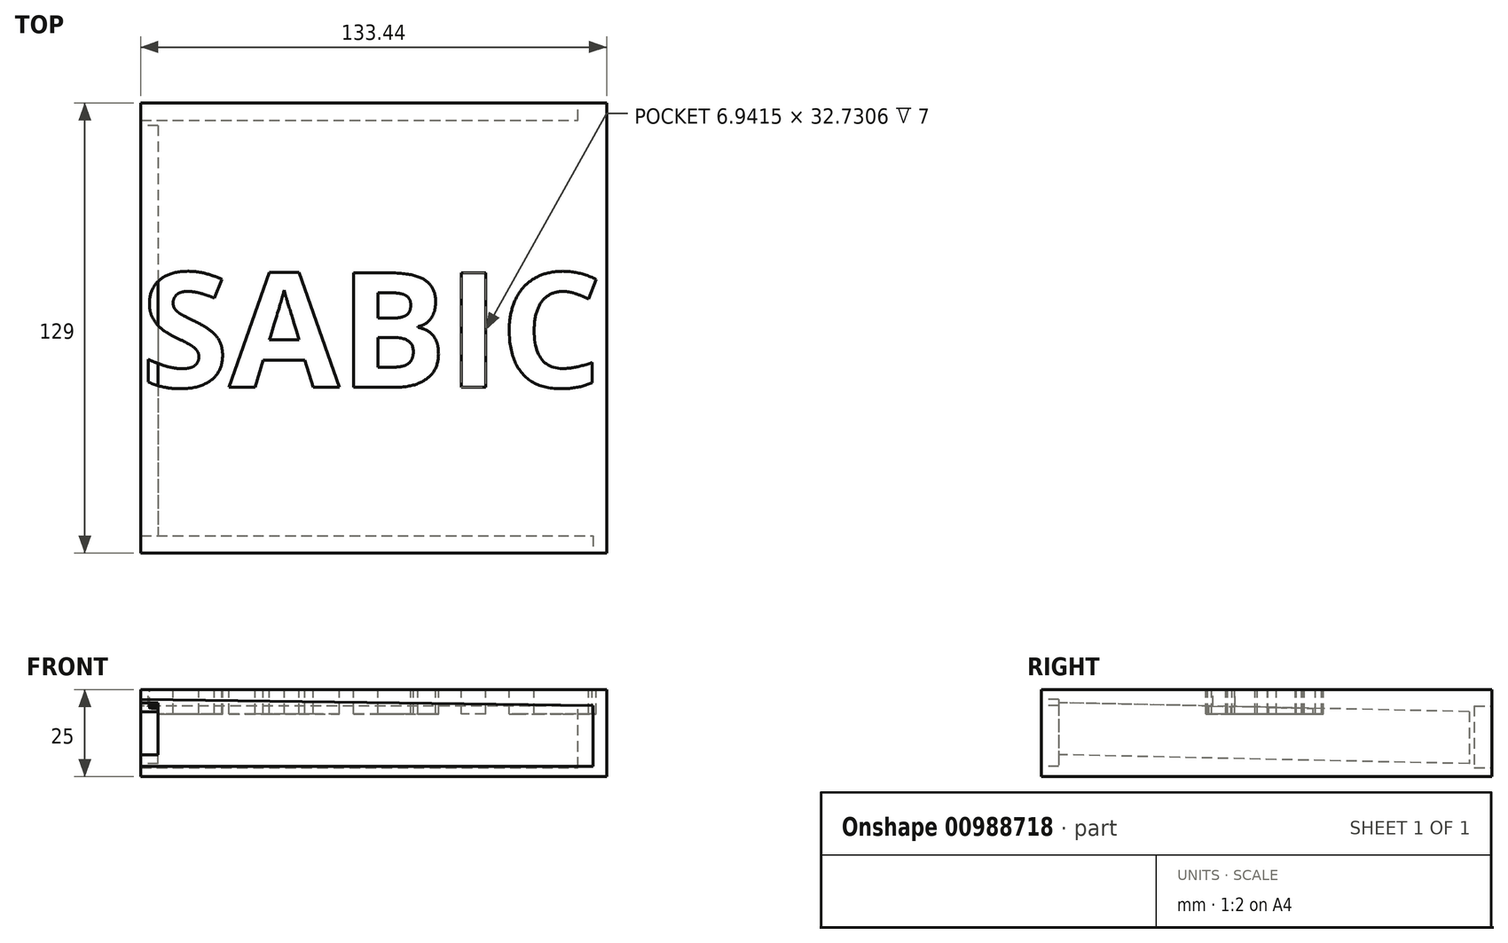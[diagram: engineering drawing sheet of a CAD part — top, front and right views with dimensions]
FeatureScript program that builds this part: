
annotation { "Feature Type Name" : "Feature", "Feature Type Description" : "" }
export const myFeature = defineFeature(function(context is Context, id is Id, definition is map)
    precondition{}
    {
        {
            var Q0;
            Q0=qCreatedBy(makeId("Top.planeOp"),FACE);
            var sketch = newSketch(context, id + "F0", { "sketchPlane" : qUnion([Q0])});
            skLineSegment(sketch, "E0.bottom", {"start": v(63.41, 63.62) * mm, "end": v(-70.03, 63.62) * mm});
            skLineSegment(sketch, "E0.top", {"start": v(63.41, -65.38) * mm, "end": v(-70.03, -65.38) * mm});
            skLineSegment(sketch, "E0.left", {"start": v(63.41, 63.62) * mm, "end": v(63.41, -65.38) * mm});
            skLineSegment(sketch, "E0.right", {"start": v(-70.03, 63.62) * mm, "end": v(-70.03, -65.38) * mm});
            skLineSegment(sketch, "E1", {"start": v(0, 63.62) * mm, "end": v(0, -65.38) * mm});
            skSolve(sketch);
        }
        {
            var Q0;
            Q0 = qSketchRegion(id + "F0", true);
            extrude(context, id + "F1", {"entities" : qUnion([Q0]), "depth" : 25 * mm, "offsetDistance" : 25 * mm});
        }
        {
            var Q0;
            Q0=makeQuery(id+"F1.opExtrude","CAP_FACE",FACE,{"disambiguationData":[OSD([sQuery(id+"F0.wireOp",EDGE,"E0.bottom"),sQuery(id+"F0.wireOp",EDGE,"E0.top"),sQuery(id+"F0.wireOp",EDGE,"E0.left"),sQuery(id+"F0.wireOp",EDGE,"E0.right")])],"isStart":false});
            var sketch = newSketch(context, id + "F2", { "sketchPlane" : qUnion([Q0])});
            skText(sketch, "E2", { "text": "SABIC", "fontName": "OpenSans-Bold.ttf"});
            const initialGuessF2  = {"E2": [-0.07003, -0.01781, 1, 0, 0.03301]};
            skSetInitialGuess(sketch, initialGuessF2);
            skSolve(sketch);
        }
        {
            var Q0;
            Q0 = qSketchRegion(id + "F2", true);
            extrude(context, id + "F3", {"entities" : qUnion([Q0]), "operationType" : NewBodyOperationType.REMOVE, "oppositeDirection" : true, "depth" : 7 * mm, "offsetDistance" : 25 * mm});
        }
        {
            var Q0;
            Q0=makeQuery(id+"F1.opExtrude","SWEPT_FACE",FACE,{"disambiguationData":[OSD([sQuery(id+"F0.wireOp",EDGE,"E0.right")])]});
            var sketch = newSketch(context, id + "F4", { "sketchPlane" : qUnion([Q0])});
            skSolve(sketch);
        }
        {
            var Q0;
            Q0=makeQuery(id+"F1.opExtrude","SWEPT_FACE",FACE,{"disambiguationData":[OSD([sQuery(id+"F0.wireOp",EDGE,"E0.top")])]});
            var sketch = newSketch(context, id + "F5", { "sketchPlane" : qUnion([Q0])});
            skLineSegment(sketch, "E3", {"start": v(-70.03, 22.16) * mm, "end": v(59.5, 20.4) * mm});
            skLineSegment(sketch, "E4", {"start": v(59.5, 20.4) * mm, "end": v(59.5, 3) * mm});
            skLineSegment(sketch, "E5", {"start": v(59.5, 3) * mm, "end": v(-70.03, 3) * mm});
            skLineSegment(sketch, "E6", {"start": v(-70.03, 3) * mm, "end": v(-70.03, 22.16) * mm});
            skSolve(sketch);
        }
        {
            var Q0;
            Q0 = qSketchRegion(id + "F5", true);
            extrude(context, id + "F6", {"entities" : qUnion([Q0]), "operationType" : NewBodyOperationType.REMOVE, "oppositeDirection" : true, "depth" : 5 * mm, "offsetDistance" : 25 * mm});
        }
        {
            var Q0;
            Q0=makeQuery(id+"F1.opExtrude","SWEPT_FACE",FACE,{"disambiguationData":[OSD([sQuery(id+"F0.wireOp",EDGE,"E0.bottom")])]});
            var sketch = newSketch(context, id + "F7", { "sketchPlane" : qUnion([Q0])});
            skLineSegment(sketch, "E7", {"start": v(70.03, 2.61) * mm, "end": v(-55.22, 2.61) * mm});
            skLineSegment(sketch, "E8", {"start": v(-55.22, 2.61) * mm, "end": v(-55.22, 20.26) * mm});
            skLineSegment(sketch, "E9", {"start": v(-56.53, 20.26) * mm, "end": v(70.03, 20.26) * mm});
            skLineSegment(sketch, "E10", {"start": v(70.03, 20.26) * mm, "end": v(70.03, 2.61) * mm});
            skSolve(sketch);
        }
        {
            var Q0;
            Q0 = qSketchRegion(id + "F7", true);
            extrude(context, id + "F8", {"entities" : qUnion([Q0]), "operationType" : NewBodyOperationType.REMOVE, "oppositeDirection" : true, "depth" : 5 * mm, "offsetDistance" : 25 * mm});
        }
        {
            var Q0;
            {var subQ0=sQuery(id+"F0.wireOp",EDGE,"E0.right");Q0=makeQuery(id+"F4.imprint","IMPRINT",FACE,{"disambiguationData":[TD([[makeQuery(id+"F4.imprint","IMPRINT",EDGE,{"derivedFrom":makeQuery(id+"F1.opExtrude","CAP_EDGE",EDGE,{"disambiguationData":[OSD([subQ0])],"isStart":true})}),1.0]])]});}
            var sketch = newSketch(context, id + "F9", { "sketchPlane" : qUnion([Q0])});
            skLineSegment(sketch, "E11", {"start": v(-57.14, 18.62) * mm, "end": v(60.42, 21.2) * mm});
            skLineSegment(sketch, "E12", {"start": v(60.42, 21.2) * mm, "end": v(-57.14, 18.62) * mm});
            skLineSegment(sketch, "E13", {"start": v(-57.14, 3.73) * mm, "end": v(60.42, 6.3) * mm});
            skLineSegment(sketch, "E14", {"start": v(60.42, 6.3) * mm, "end": v(60.42, 21.2) * mm});
            skLineSegment(sketch, "E15", {"start": v(-57.14, 18.62) * mm, "end": v(-57.14, 3.73) * mm});
            skSolve(sketch);
        }
        {
            var Q0;
            Q0 = qSketchRegion(id + "F9", true);
            extrude(context, id + "F10", {"entities" : qUnion([Q0]), "operationType" : NewBodyOperationType.REMOVE, "oppositeDirection" : true, "depth" : 5 * mm, "offsetDistance" : 25 * mm});
        }
    });
